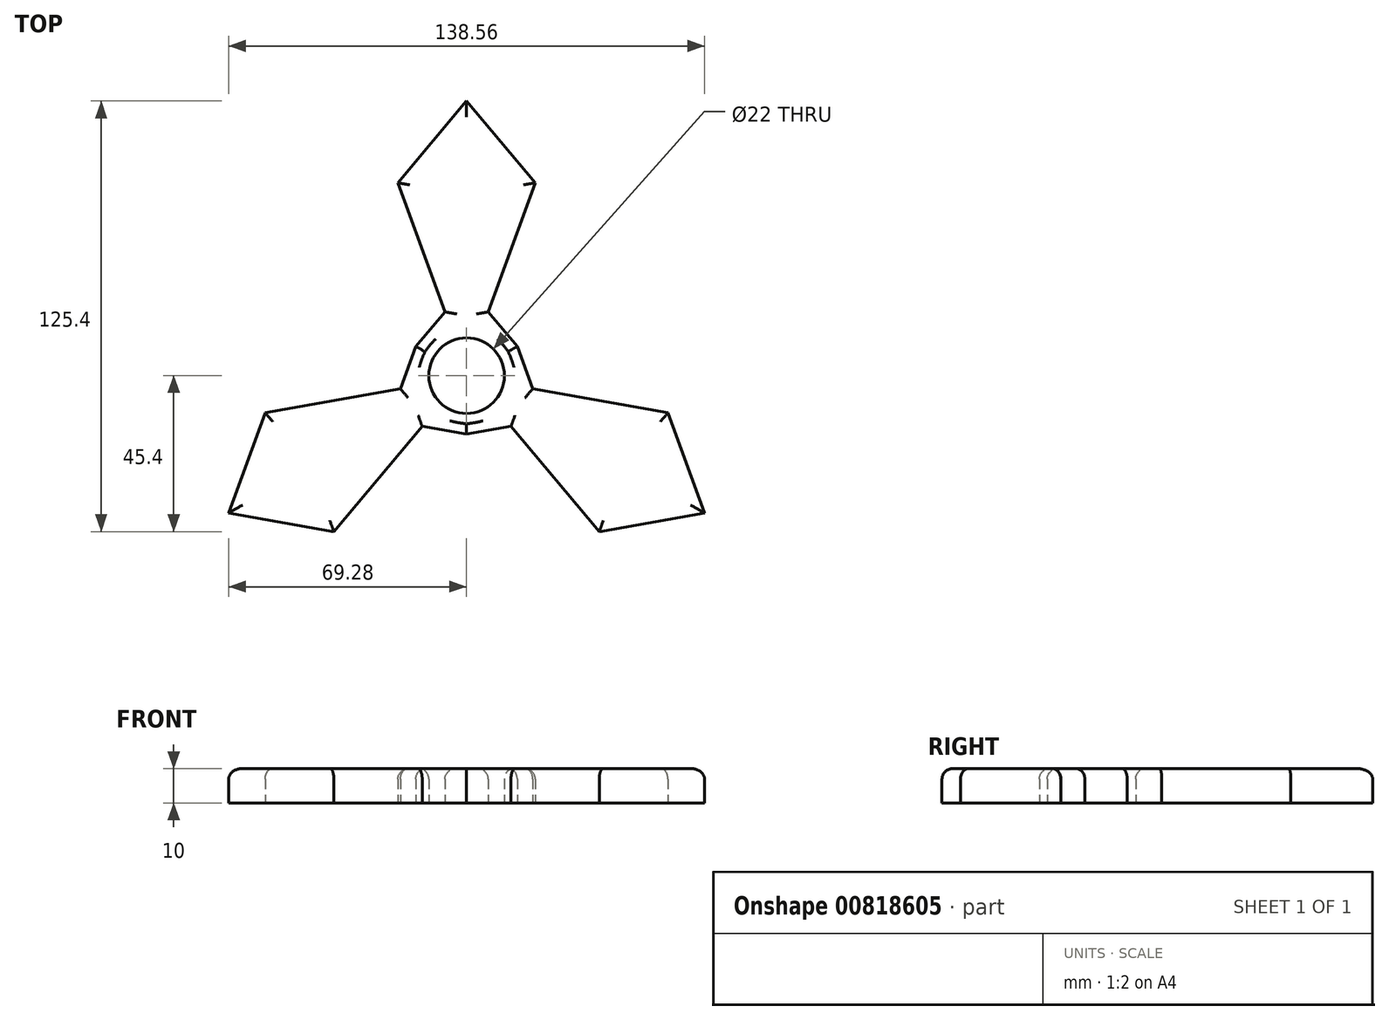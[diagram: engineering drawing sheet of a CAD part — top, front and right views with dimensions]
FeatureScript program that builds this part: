
annotation { "Feature Type Name" : "Feature", "Feature Type Description" : "" }
export const myFeature = defineFeature(function(context is Context, id is Id, definition is map)
    precondition{}
    {
        {
            var Q0;
            Q0=qCreatedBy(makeId("Top.planeOp"),FACE);
            var sketch = newSketch(context, id + "F0", { "sketchPlane" : qUnion([Q0])});
            skCircle(sketch, "E0", {"center": v(0, 0) * mm, "radius": 4 * mm});
            skCircle(sketch, "E1", {"center": v(0, 0) * mm, "radius": 11 * mm});
            skLineSegment(sketch, "E2", {"start": v(0, 80) * mm, "end": v(20, 56.16) * mm});
            skLineSegment(sketch, "E3", {"start": v(20, 56.16) * mm, "end": v(6.32, 18.58) * mm});
            skLineSegment(sketch, "E4", {"start": v(6.32, 18.58) * mm, "end": v(14.76, 8.52) * mm});
            skLineSegment(sketch, "E5", {"start": v(0, 0) * mm, "end": v(14.76, 8.52) * mm, "construction": true});
            skLineSegment(sketch, "E6.MirrorCS", {"start": v(0, 80) * mm, "end": v(-20, 56.16) * mm});
            skLineSegment(sketch, "E7.MirrorCS", {"start": v(-20, 56.16) * mm, "end": v(-6.32, 18.58) * mm});
            skLineSegment(sketch, "E8.MirrorCS", {"start": v(-6.32, 18.58) * mm, "end": v(-14.76, 8.52) * mm});
            skLineSegment(sketch, "E9.MirrorCS", {"start": v(0, 0) * mm, "end": v(-14.76, 8.52) * mm, "construction": true});
            skLineSegment(sketch, "E10.1.0", {"start": v(-19.25, -3.82) * mm, "end": v(-14.76, 8.52) * mm});
            skLineSegment(sketch, "E10.1.1", {"start": v(-69.28, -40) * mm, "end": v(-38.64, -45.4) * mm});
            skLineSegment(sketch, "E10.1.2", {"start": v(-69.28, -40) * mm, "end": v(-58.64, -10.76) * mm});
            skLineSegment(sketch, "E10.1.3", {"start": v(-38.64, -45.4) * mm, "end": v(-12.93, -14.76) * mm});
            skLineSegment(sketch, "E10.1.4", {"start": v(-58.64, -10.76) * mm, "end": v(-19.25, -3.82) * mm});
            skLineSegment(sketch, "E10.1.5", {"start": v(-12.93, -14.76) * mm, "end": v(0, -17.04) * mm});
            skLineSegment(sketch, "E10.1.6", {"start": v(-38.64, -45.4) * mm, "end": v(-12.93, -14.76) * mm});
            skLineSegment(sketch, "E10.1.7", {"start": v(-19.25, -3.82) * mm, "end": v(-14.76, 8.52) * mm});
            skLineSegment(sketch, "E10.1.8", {"start": v(-58.64, -10.76) * mm, "end": v(-19.25, -3.82) * mm});
            skLineSegment(sketch, "E10.1.9", {"start": v(-69.28, -40) * mm, "end": v(-38.64, -45.4) * mm});
            skLineSegment(sketch, "E10.1.10", {"start": v(-69.28, -40) * mm, "end": v(-58.64, -10.76) * mm});
            skLineSegment(sketch, "E10.1.11", {"start": v(-12.93, -14.76) * mm, "end": v(0, -17.04) * mm});
            skLineSegment(sketch, "E10.2.0", {"start": v(12.93, -14.76) * mm, "end": v(0, -17.04) * mm});
            skLineSegment(sketch, "E10.2.1", {"start": v(69.28, -40) * mm, "end": v(58.64, -10.76) * mm});
            skLineSegment(sketch, "E10.2.2", {"start": v(69.28, -40) * mm, "end": v(38.64, -45.4) * mm});
            skLineSegment(sketch, "E10.2.3", {"start": v(58.64, -10.76) * mm, "end": v(19.25, -3.82) * mm});
            skLineSegment(sketch, "E10.2.4", {"start": v(38.64, -45.4) * mm, "end": v(12.93, -14.76) * mm});
            skLineSegment(sketch, "E10.2.5", {"start": v(19.25, -3.82) * mm, "end": v(14.76, 8.52) * mm});
            skLineSegment(sketch, "E10.2.6", {"start": v(58.64, -10.76) * mm, "end": v(19.25, -3.82) * mm});
            skLineSegment(sketch, "E10.2.7", {"start": v(12.93, -14.76) * mm, "end": v(0, -17.04) * mm});
            skLineSegment(sketch, "E10.2.8", {"start": v(38.64, -45.4) * mm, "end": v(12.93, -14.76) * mm});
            skLineSegment(sketch, "E10.2.9", {"start": v(69.28, -40) * mm, "end": v(58.64, -10.76) * mm});
            skLineSegment(sketch, "E10.2.10", {"start": v(69.28, -40) * mm, "end": v(38.64, -45.4) * mm});
            skLineSegment(sketch, "E10.2.11", {"start": v(19.25, -3.82) * mm, "end": v(14.76, 8.52) * mm});
            skSolve(sketch);
        }
        {
            var Q0;
            Q0=makeQuery(id+"F0.imprint","IMPRINT",FACE,{"disambiguationData":[TD([[makeQuery(id+"F0.imprint","IMPRINT",EDGE,{"derivedFrom":sQuery(id+"F0.wireOp",EDGE,"E4")}),-1.0]])]});
            extrude(context, id + "F1", {"entities" : qUnion([Q0]), "depth" : 10 * mm, "offsetDistance" : 25 * mm});
        }
        {
            var Q0;
            Q0=makeQuery(id+"F1.opExtrude","CAP_FACE",FACE,{"disambiguationData":[OSD([sQuery(id+"F0.wireOp",EDGE,"E4"),sQuery(id+"F0.wireOp",EDGE,"E6.MirrorCS"),sQuery(id+"F0.wireOp",EDGE,"E2"),sQuery(id+"F0.wireOp",EDGE,"E7.MirrorCS"),sQuery(id+"F0.wireOp",EDGE,"E3"),sQuery(id+"F0.wireOp",EDGE,"E8.MirrorCS"),sQuery(id+"F0.wireOp",EDGE,"E1"),sQuery(id+"F0.wireOp",EDGE,"E10.1.6"),sQuery(id+"F0.wireOp",EDGE,"E10.1.7"),sQuery(id+"F0.wireOp",EDGE,"E10.1.8"),sQuery(id+"F0.wireOp",EDGE,"E10.1.9"),sQuery(id+"F0.wireOp",EDGE,"E10.1.10"),sQuery(id+"F0.wireOp",EDGE,"E10.1.11"),sQuery(id+"F0.wireOp",EDGE,"E10.2.6"),sQuery(id+"F0.wireOp",EDGE,"E10.2.7"),sQuery(id+"F0.wireOp",EDGE,"E10.2.8"),sQuery(id+"F0.wireOp",EDGE,"E10.2.9"),sQuery(id+"F0.wireOp",EDGE,"E10.2.10"),sQuery(id+"F0.wireOp",EDGE,"E10.2.11")])],"isStart":false});
            fillet(context, id + "F2", {"entities" : qUnion([Q0]), "radius" : 3 * mm, "tangentPropagation" : true, "allowEdgeOverflow" : false});
        }
    });
